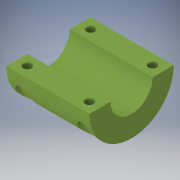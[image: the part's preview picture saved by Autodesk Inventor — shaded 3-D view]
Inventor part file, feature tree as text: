
AUTODESK INVENTOR PART (.ipt)
format: ipt  version: 2018 (Build 220112000, 112)  size: 175,104 bytes
history: native  units: in
note: dims shown in document units (in); Inventor stores cm internally (conversion verified against a paired STEP export)
features: extrude x3, plane x3, sketch x3
ambient origin geometry x8: Origin, YZ Plane, XZ Plane, XY Plane, X Axis, Y Axis, Z Axis, Center Point
bodies: Solid1 (feature_tree)
feature tree (9):
  extrude  "Extrusion1"  Depth=1.9685in TaperAngle=0.0deg
  plane  "Work Plane1"
  plane  "Work Plane2"
  extrude  "Extrusion13"  Depth=0.5in
  plane  "Work Plane3"
  extrude  "Extrusion14"  Depth=0.5in
  sketch  "Sketch2"  dims[d5=180.0deg d7=1.9685in d8=0.0in]
  sketch  "Sketch15"  dims[d122=180.0deg d123=0.5in]
  sketch  "Sketch16"  dims[d124=1.0in d125=0.5in d127=0.0in d128=0.19in d129=0.19in d130=0.19in d131=0.19in d132=0.25in d133=0.25in d134=0.25in d135=0.25in d136=0.25in d137=0.25in d138=0.25in d139=0.25in d140=1.0in d141=0.0in d142=-0.5348in d143=0.4in d144=0.4in d145=0.4in d146=0.4in d147=0.4in d148=0.5in d149=0.0in d150=0.0in]
